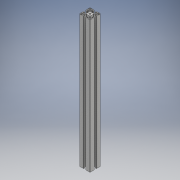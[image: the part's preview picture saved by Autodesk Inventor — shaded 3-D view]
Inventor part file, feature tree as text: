
AUTODESK INVENTOR PART (.ipt)
format: ipt  version: 2018.3 (Build 223284000, 284)  size: 316,928 bytes
history: native  units: mm
features: extrude x1, sketch x1
ambient origin geometry x8: Origin, YZ Plane, XZ Plane, XY Plane, X Axis, Y Axis, Z Axis, Center Point
bodies: Body1 (feature_tree)
feature tree (2):
  extrude  "Extrusión1"  [1 undecoded]
  sketch  "Boceto1"  dims[d0=500.0mm d1=0.0mm]
note: 1 required parameter value undecoded (feature->parameter linkage not recoverable at this tier; creation-order binding heuristic only, values carry confidence <= 0.55)
